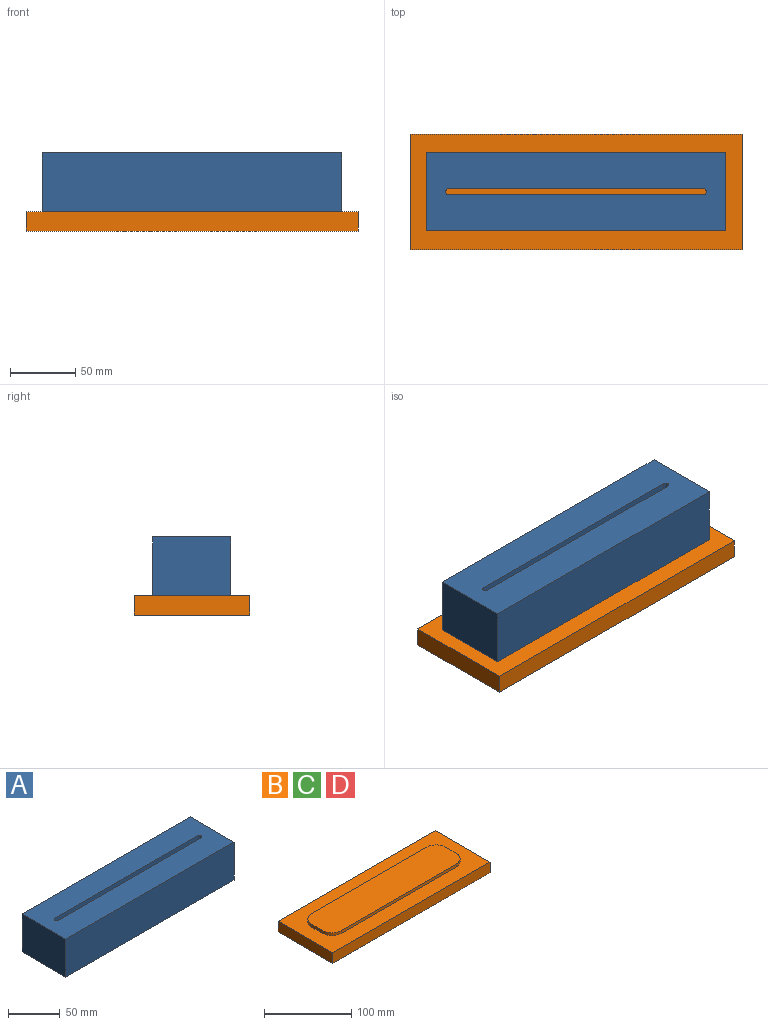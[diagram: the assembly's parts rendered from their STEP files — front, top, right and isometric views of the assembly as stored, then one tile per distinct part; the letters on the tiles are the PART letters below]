
ASSEMBLY  parts=4 mates=1
PART A: 23 faces, bbox 230x60x45 mm
  f0: plane 230x45mm, normal (0,-1,0), area 10350mm2, adj f1,f3,f4,f5
  f1: plane 60x45mm, normal (1,0,0), area 2700mm2, adj f0,f2,f4,f5
  f2: plane 230x45mm, normal (0,1,0), area 10350mm2, adj f1,f3,f4,f5
  f3: plane 60x45mm, normal (-1,0,0), area 2700mm2, adj f0,f2,f4,f5
  f4: plane 230x60mm, normal (0,0,-1), area 3481.1mm2, adj f0,f1,f2,f3,f6,f7,f8,f9
  f5: plane 230x60mm, normal (0,0,1), area 12903.4mm2, adj f0,f1,f2,f3,f15,f16,f17,f18
  f6: plane 38x22mm, normal (1,0,0), area 836mm2, adj f4,f7,f13,f14
  f7: cylinder r=13mm len=38mm, axis (0,0,-1), area 776mm2, adj f4,f6,f8,f14
  f8: plane 192x38mm, normal (0,-1,0), area 7296mm2, adj f4,f7,f9,f14
  f9: cylinder r=13mm len=38mm, axis (0,0,-1), area 776mm2, adj f4,f8,f10,f14
  f10: plane 38x22mm, normal (-1,0,0), area 836mm2, adj f4,f9,f11,f14
  f11: cylinder r=13mm len=38mm, axis (0,0,-1), area 776mm2, adj f4,f10,f12,f14
  f12: plane 192x38mm, normal (0,1,0), area 7296mm2, adj f4,f11,f13,f14
  f13: cylinder r=13mm len=38mm, axis (0,0,-1), area 776mm2, adj f4,f6,f12,f14
  f14: plane 218x48mm, normal (0,0,-1), area 9422.4mm2, adj f6,f7,f8,f9,f10,f11,f12,f13
  f15: plane 196x7mm, normal (0,-1,0), area 1372mm2, adj f5,f14,f16,f22
  f16: cylinder r=2mm len=7mm, axis (0,0,1), area 22mm2, adj f5,f14,f15,f17
  f17: plane 7x0.5mm, normal (1,0,0), area 3.5mm2, adj f5,f14,f16,f18
  f18: cylinder r=2mm len=7mm, axis (0,0,1), area 22mm2, adj f5,f14,f17,f19
  f19: plane 196x7mm, normal (0,1,0), area 1372mm2, adj f5,f14,f18,f20
  f20: cylinder r=2mm len=7mm, axis (0,0,1), area 22mm2, adj f5,f14,f19,f21
  f21: plane 7x0.5mm, normal (-1,0,0), area 3.5mm2, adj f5,f14,f20,f22
  f22: cylinder r=2mm len=7mm, axis (0,0,1), area 22mm2, adj f5,f14,f15,f21
PART B: 15 faces, bbox 255x89x19 mm
  f0: plane 255x89mm, normal (0,0,1), area 12580.6mm2, adj f1,f2,f3,f4,f6,f7,f8,f9
  f1: plane 255x15mm, normal (0,-1,0), area 3825mm2, adj f0,f2,f4,f5
  f2: plane 89x15mm, normal (1,0,0), area 1335mm2, adj f0,f1,f3,f5
  f3: plane 255x15mm, normal (0,1,0), area 3825mm2, adj f0,f2,f4,f5
  f4: plane 89x15mm, normal (-1,0,0), area 1335mm2, adj f0,f1,f3,f5
  f5: plane 255x89mm, normal (0,0,-1), area 22695mm2, adj f1,f2,f3,f4
  f6: plane 17.5x4mm, normal (-1,0,0), area 70mm2, adj f0,f7,f13,f14
  f7: cylinder r=15mm len=15mm, axis (0,0,-1), area 94.2mm2, adj f0,f6,f8,f14
  f8: plane 187x4mm, normal (0,-1,0), area 748mm2, adj f0,f7,f9,f14
  f9: cylinder r=15mm len=15mm, axis (0,0,-1), area 94.2mm2, adj f0,f8,f10,f14
  f10: plane 17.5x4mm, normal (1,0,0), area 70mm2, adj f0,f9,f11,f14
  f11: cylinder r=15mm len=15mm, axis (0,0,-1), area 94.2mm2, adj f0,f10,f12,f14
  f12: plane 187x4mm, normal (0,1,0), area 748mm2, adj f0,f11,f13,f14
  f13: cylinder r=15mm len=15mm, axis (0,0,-1), area 94.2mm2, adj f0,f6,f12,f14
  f14: plane 217x47.5mm, normal (0,0,1), area 10114.4mm2, adj f6,f7,f8,f9,f10,f11,f12,f13
PART C: same geometry as B
PART D: same geometry as B
PLACE A t=(-34.1,-64.71,-17.41)mm
PLACE B t=(-34.1,-64.96,27.59)mm fixed
PLACE C t=(-34.1,-64.96,27.59)mm
PLACE D t=(-34.1,-64.96,27.59)mm
MATE slider B.f0 <-> A.f4  axis (0,0,1) through (-34.1,-88.71,-62.41)mm
